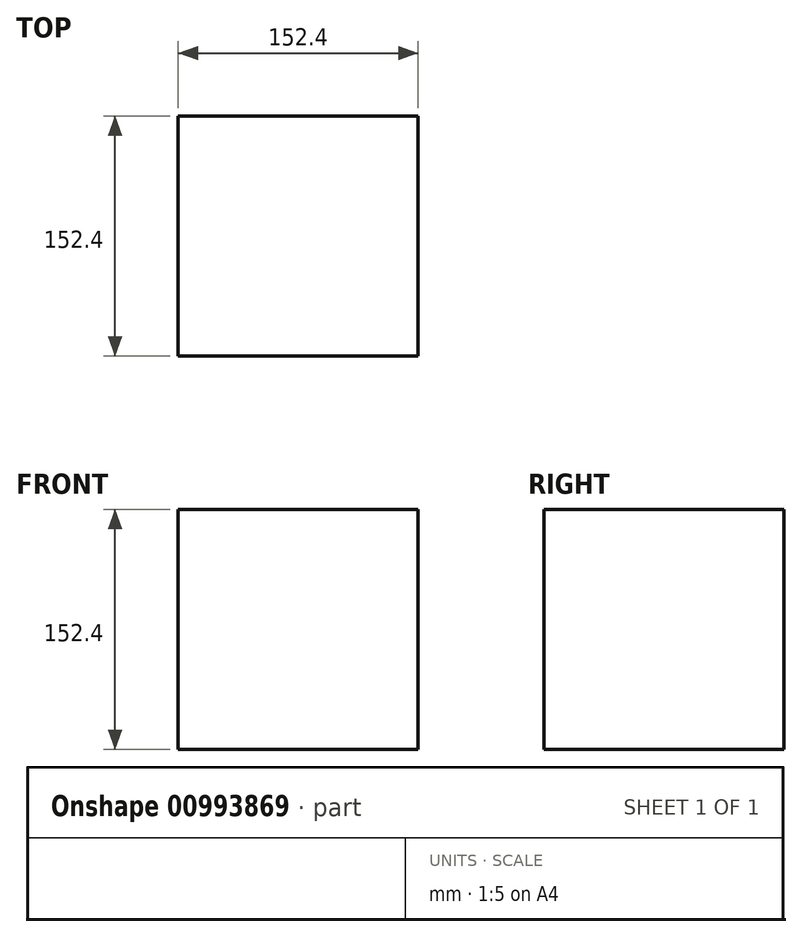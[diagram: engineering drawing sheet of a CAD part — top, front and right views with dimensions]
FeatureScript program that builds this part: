
annotation { "Feature Type Name" : "Feature", "Feature Type Description" : "" }
export const myFeature = defineFeature(function(context is Context, id is Id, definition is map)
    precondition{}
    {
        {
            var Q0;
            Q0=qCreatedBy(makeId("Top.planeOp"),FACE);
            var sketch = newSketch(context, id + "F0", { "sketchPlane" : qUnion([Q0])});
            skLineSegment(sketch, "E0.bottom", {"start": v(-76.2, -76.2) * mm, "end": v(76.2, -76.2) * mm});
            skLineSegment(sketch, "E0.top", {"start": v(-76.2, 76.2) * mm, "end": v(76.2, 76.2) * mm});
            skLineSegment(sketch, "E0.left", {"start": v(-76.2, -76.2) * mm, "end": v(-76.2, 76.2) * mm});
            skLineSegment(sketch, "E0.right", {"start": v(76.2, -76.2) * mm, "end": v(76.2, 76.2) * mm});
            skPoint(sketch, "E0.middle", {"position": v(0, 0) * mm});
            skSolve(sketch);
        }
        {
            var Q0;
            Q0 = qSketchRegion(id + "F0", true);
            extrude(context, id + "F1", {"entities" : qUnion([Q0]), "depth" : 152.4 * mm, "offsetDistance" : 25 * mm});
        }
    });
